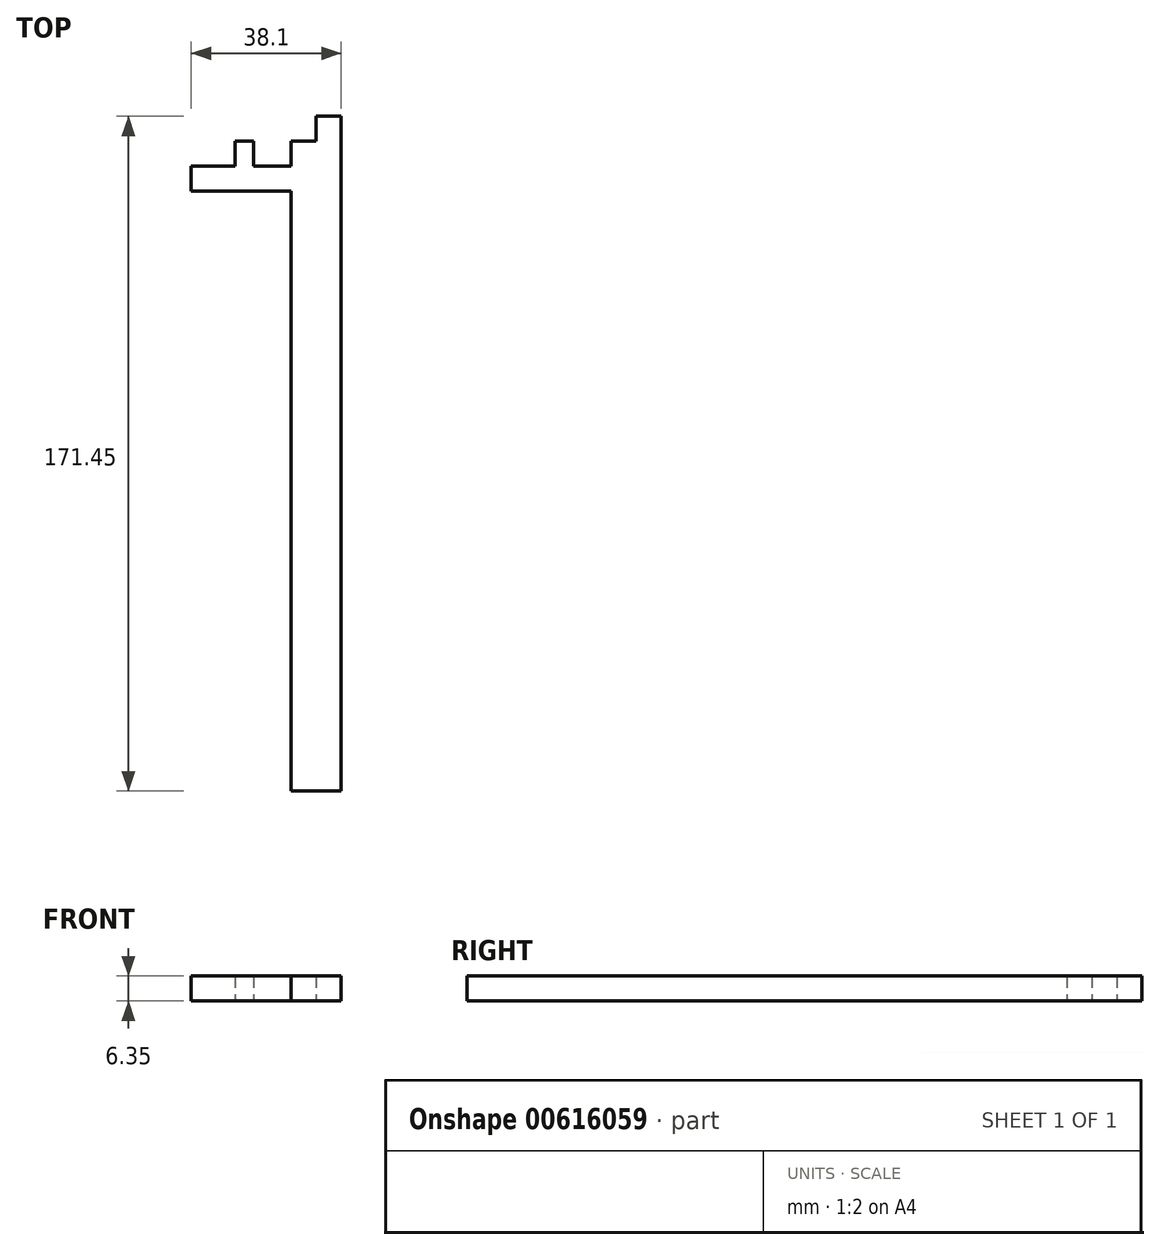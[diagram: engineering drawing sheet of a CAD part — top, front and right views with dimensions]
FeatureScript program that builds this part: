
annotation { "Feature Type Name" : "Feature", "Feature Type Description" : "" }
export const myFeature = defineFeature(function(context is Context, id is Id, definition is map)
    precondition{}
    {
        {
            var Q0;
            Q0=qCreatedBy(makeId("Top.planeOp"),FACE);
            var sketch = newSketch(context, id + "F0", { "sketchPlane" : qUnion([Q0])});
            skLineSegment(sketch, "E0.bottom", {"start": v(-46.96, 6.01) * mm, "end": v(-59.66, 6.01) * mm});
            skLineSegment(sketch, "E0.top", {"start": v(-46.96, -146.39) * mm, "end": v(-59.66, -146.39) * mm});
            skLineSegment(sketch, "E0.left", {"start": v(-46.96, 6.01) * mm, "end": v(-46.96, -146.39) * mm});
            skLineSegment(sketch, "E0.right", {"start": v(-59.66, 6.01) * mm, "end": v(-59.66, -146.39) * mm});
            skPoint(sketch, "E0.middle", {"position": v(-53.31, -70.19) * mm});
            skLineSegment(sketch, "E1.bottom", {"start": v(-46.96, 6.01) * mm, "end": v(-85.06, 6.01) * mm});
            skLineSegment(sketch, "E1.top", {"start": v(-46.96, 12.36) * mm, "end": v(-85.06, 12.36) * mm});
            skLineSegment(sketch, "E1.left", {"start": v(-46.96, 6.01) * mm, "end": v(-46.96, 12.36) * mm});
            skLineSegment(sketch, "E1.right", {"start": v(-85.06, 6.01) * mm, "end": v(-85.06, 12.36) * mm});
            skLineSegment(sketch, "E2.bottom", {"start": v(-46.96, 12.36) * mm, "end": v(-59.66, 12.36) * mm});
            skLineSegment(sketch, "E2.top", {"start": v(-46.96, 18.71) * mm, "end": v(-59.66, 18.71) * mm});
            skLineSegment(sketch, "E2.left", {"start": v(-46.96, 12.36) * mm, "end": v(-46.96, 18.71) * mm});
            skLineSegment(sketch, "E2.right", {"start": v(-59.66, 12.36) * mm, "end": v(-59.66, 18.71) * mm});
            skLineSegment(sketch, "E3.bottom", {"start": v(-46.96, 18.71) * mm, "end": v(-53.31, 18.71) * mm});
            skLineSegment(sketch, "E3.top", {"start": v(-46.96, 25.06) * mm, "end": v(-53.31, 25.06) * mm});
            skLineSegment(sketch, "E3.left", {"start": v(-46.96, 18.71) * mm, "end": v(-46.96, 25.06) * mm});
            skLineSegment(sketch, "E3.right", {"start": v(-53.31, 18.71) * mm, "end": v(-53.31, 25.06) * mm});
            skLineSegment(sketch, "E4.bottom", {"start": v(-69.19, 12.36) * mm, "end": v(-73.95, 12.36) * mm});
            skLineSegment(sketch, "E4.top", {"start": v(-69.19, 18.71) * mm, "end": v(-73.95, 18.71) * mm});
            skLineSegment(sketch, "E4.left", {"start": v(-69.19, 12.36) * mm, "end": v(-69.19, 18.71) * mm});
            skLineSegment(sketch, "E4.right", {"start": v(-73.95, 12.36) * mm, "end": v(-73.95, 18.71) * mm});
            skSolve(sketch);
        }
        {
            var Q0;
            Q0 = qSketchRegion(id + "F0", true);
            extrude(context, id + "F1", {"entities" : qUnion([Q0]), "depth" : 6.35 * mm, "offsetDistance" : 25.4 * mm});
        }
    });
